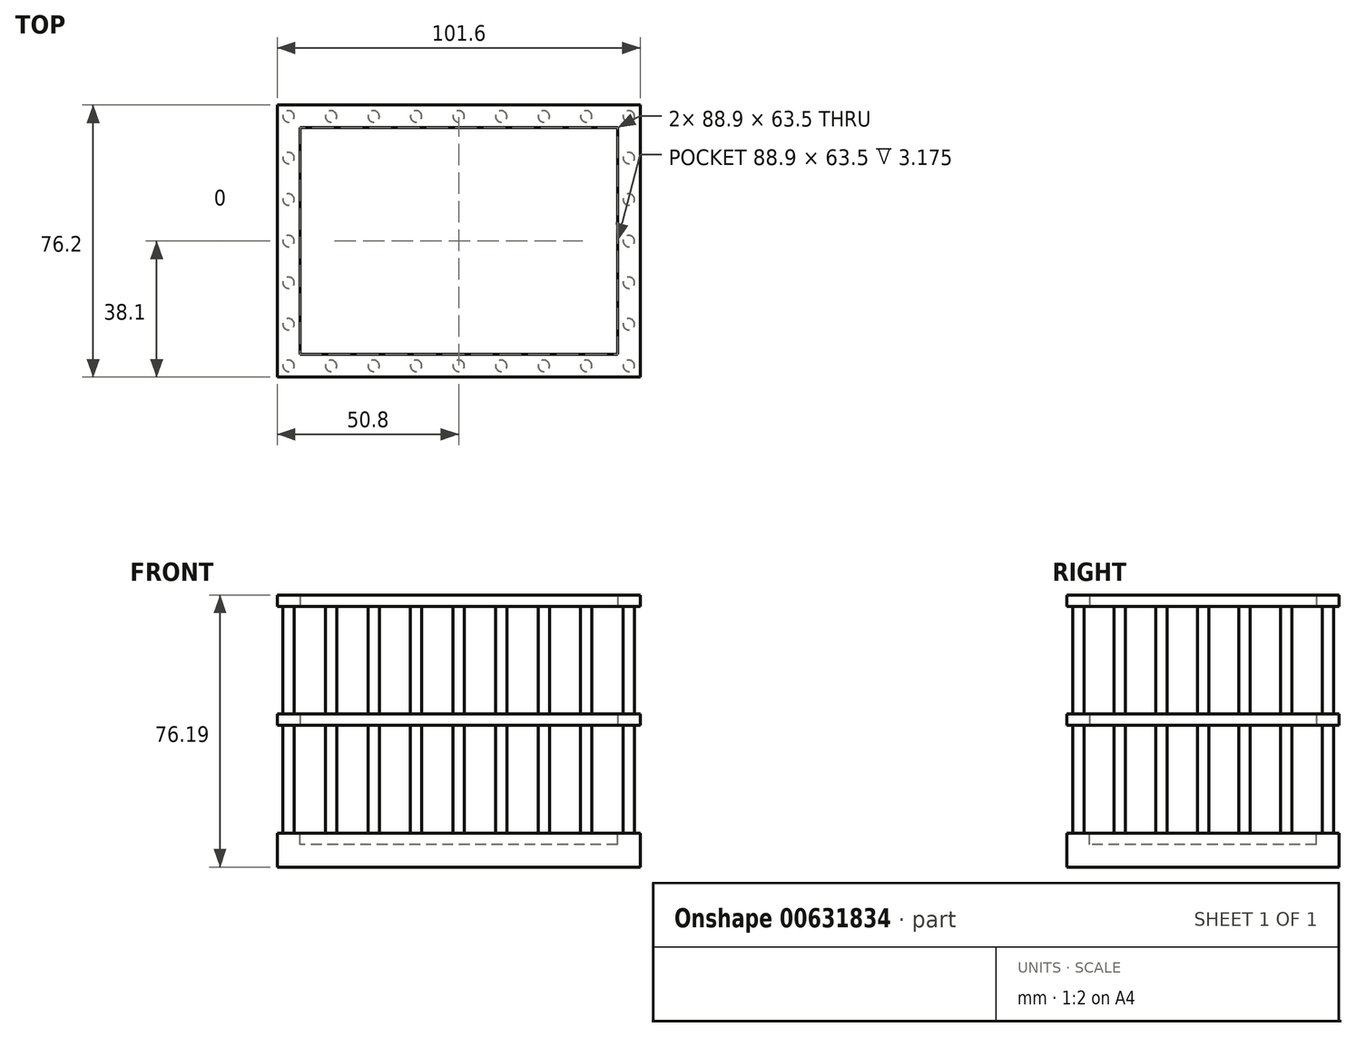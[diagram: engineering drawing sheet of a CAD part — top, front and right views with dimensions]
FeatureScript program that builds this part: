
annotation { "Feature Type Name" : "Feature", "Feature Type Description" : "" }
export const myFeature = defineFeature(function(context is Context, id is Id, definition is map)
    precondition{}
    {
        {
            var Q0;
            Q0=qCreatedBy(makeId("Top.planeOp"),FACE);
            var sketch = newSketch(context, id + "F0", { "sketchPlane" : qUnion([Q0])});
            skLineSegment(sketch, "E0.bottom", {"start": v(-101.6, 76.2) * mm, "end": v(0, 76.2) * mm});
            skLineSegment(sketch, "E0.top", {"start": v(-101.6, 0) * mm, "end": v(0, 0) * mm});
            skLineSegment(sketch, "E0.left", {"start": v(-101.6, 76.2) * mm, "end": v(-101.6, 0) * mm});
            skLineSegment(sketch, "E0.right", {"start": v(0, 76.2) * mm, "end": v(0, 0) * mm});
            skLineSegment(sketch, "E1.bottom", {"start": v(-95.25, 69.85) * mm, "end": v(-6.35, 69.85) * mm});
            skLineSegment(sketch, "E1.top", {"start": v(-95.25, 6.35) * mm, "end": v(-6.35, 6.35) * mm});
            skLineSegment(sketch, "E1.left", {"start": v(-95.25, 69.85) * mm, "end": v(-95.25, 6.35) * mm});
            skLineSegment(sketch, "E1.right", {"start": v(-6.35, 69.85) * mm, "end": v(-6.35, 6.35) * mm});
            skLineSegment(sketch, "E2", {"start": v(-95.25, 6.35) * mm, "end": v(-6.35, 69.85) * mm, "construction": true});
            skLineSegment(sketch, "E3", {"start": v(-101.6, 76.2) * mm, "end": v(0, 0) * mm, "construction": true});
            skPoint(sketch, "E4", {"position": v(-50.8, 38.1) * mm});
            skLineSegment(sketch, "E5", {"start": v(-95.25, 38.1) * mm, "end": v(-101.6, 38.1) * mm, "construction": true});
            skLineSegment(sketch, "E6", {"start": v(-50.8, 69.85) * mm, "end": v(-50.8, 76.2) * mm, "construction": true});
            skSolve(sketch);
        }
        {
            var Q0;
            Q0 = qSketchRegion(id + "F0", true);
            extrude(context, id + "F1", {"entities" : qUnion([Q0]), "endBound" : BoundingType.SYMMETRIC, "depth" : 3.17 * mm, "offsetDistance" : 25.4 * mm});
        }
        {
            var Q0;
            Q0=qCreatedBy(makeId("Top.planeOp"),FACE);
            var sketch = newSketch(context, id + "F2", { "sketchPlane" : qUnion([Q0])});
            skCircle(sketch, "E7", {"center": v(-98.42, 3.18) * mm, "radius": 1.59 * mm});
            skCircle(sketch, "E8", {"center": v(-86.52, 3.18) * mm, "radius": 1.59 * mm});
            skCircle(sketch, "E9", {"center": v(-74.61, 3.18) * mm, "radius": 1.59 * mm});
            skCircle(sketch, "E10", {"center": v(-38.9, 73.02) * mm, "radius": 1.59 * mm});
            skCircle(sketch, "E11", {"center": v(-98.42, 26.46) * mm, "radius": 1.59 * mm});
            skCircle(sketch, "E12", {"center": v(-98.42, 14.82) * mm, "radius": 1.59 * mm});
            skCircle(sketch, "E13", {"center": v(-62.7, 73.02) * mm, "radius": 1.59 * mm});
            skCircle(sketch, "E14", {"center": v(-3.17, 49.74) * mm, "radius": 1.59 * mm});
            skCircle(sketch, "E15", {"center": v(-3.17, 61.38) * mm, "radius": 1.59 * mm});
            skCircle(sketch, "E16", {"center": v(-3.17, 73.02) * mm, "radius": 1.59 * mm});
            skCircle(sketch, "E17", {"center": v(-15.08, 73.02) * mm, "radius": 1.59 * mm});
            skCircle(sketch, "E18", {"center": v(-50.8, 3.18) * mm, "radius": 1.59 * mm});
            skCircle(sketch, "E19", {"center": v(-62.7, 3.18) * mm, "radius": 1.59 * mm});
            skCircle(sketch, "E20", {"center": v(-26.99, 73.02) * mm, "radius": 1.59 * mm});
            skCircle(sketch, "E21", {"center": v(-3.17, 14.82) * mm, "radius": 1.59 * mm});
            skCircle(sketch, "E22", {"center": v(-3.17, 26.46) * mm, "radius": 1.59 * mm});
            skCircle(sketch, "E23", {"center": v(-3.17, 38.1) * mm, "radius": 1.59 * mm});
            skCircle(sketch, "E24", {"center": v(-3.17, 3.18) * mm, "radius": 1.59 * mm});
            skCircle(sketch, "E25", {"center": v(-15.08, 3.18) * mm, "radius": 1.59 * mm});
            skCircle(sketch, "E26", {"center": v(-26.99, 3.18) * mm, "radius": 1.59 * mm});
            skCircle(sketch, "E27", {"center": v(-38.9, 3.18) * mm, "radius": 1.59 * mm});
            skCircle(sketch, "E28", {"center": v(-98.43, 49.74) * mm, "radius": 1.59 * mm});
            skCircle(sketch, "E29", {"center": v(-74.61, 73.02) * mm, "radius": 1.59 * mm});
            skCircle(sketch, "E30", {"center": v(-98.43, 38.1) * mm, "radius": 1.59 * mm});
            skCircle(sketch, "E31", {"center": v(-50.8, 73.02) * mm, "radius": 1.59 * mm});
            skCircle(sketch, "E32", {"center": v(-98.42, 73.02) * mm, "radius": 1.59 * mm});
            skCircle(sketch, "E33", {"center": v(-86.52, 73.02) * mm, "radius": 1.59 * mm});
            skCircle(sketch, "E34", {"center": v(-98.43, 61.38) * mm, "radius": 1.59 * mm});
            skLineSegment(sketch, "E35", {"start": v(-98.43, 73.02) * mm, "end": v(-98.43, 61.38) * mm, "construction": true});
            skLineSegment(sketch, "E36", {"start": v(-98.43, 61.38) * mm, "end": v(-98.43, 49.74) * mm, "construction": true});
            skLineSegment(sketch, "E37", {"start": v(-98.43, 49.74) * mm, "end": v(-98.43, 38.1) * mm, "construction": true});
            skLineSegment(sketch, "E38", {"start": v(-98.43, 38.1) * mm, "end": v(-98.43, 26.46) * mm, "construction": true});
            skLineSegment(sketch, "E39", {"start": v(-98.43, 26.46) * mm, "end": v(-98.43, 14.82) * mm, "construction": true});
            skLineSegment(sketch, "E40", {"start": v(-98.43, 14.82) * mm, "end": v(-98.43, 3.18) * mm, "construction": true});
            skLineSegment(sketch, "E41", {"start": v(-3.17, 73.02) * mm, "end": v(-3.17, 61.38) * mm, "construction": true});
            skLineSegment(sketch, "E42", {"start": v(-3.17, 61.38) * mm, "end": v(-3.17, 49.74) * mm, "construction": true});
            skLineSegment(sketch, "E43", {"start": v(-3.17, 49.74) * mm, "end": v(-3.17, 38.1) * mm, "construction": true});
            skLineSegment(sketch, "E44", {"start": v(-3.17, 38.1) * mm, "end": v(-3.17, 26.46) * mm, "construction": true});
            skLineSegment(sketch, "E45", {"start": v(-3.17, 26.46) * mm, "end": v(-3.17, 14.82) * mm, "construction": true});
            skLineSegment(sketch, "E46", {"start": v(-3.17, 14.82) * mm, "end": v(-3.17, 3.18) * mm, "construction": true});
            skLineSegment(sketch, "E47", {"start": v(-3.17, 3.18) * mm, "end": v(-15.08, 3.18) * mm, "construction": true});
            skLineSegment(sketch, "E48", {"start": v(-15.08, 3.18) * mm, "end": v(-26.99, 3.18) * mm, "construction": true});
            skLineSegment(sketch, "E49", {"start": v(-26.99, 3.18) * mm, "end": v(-38.9, 3.18) * mm, "construction": true});
            skLineSegment(sketch, "E50", {"start": v(-38.9, 3.18) * mm, "end": v(-50.8, 3.18) * mm, "construction": true});
            skLineSegment(sketch, "E51", {"start": v(-50.8, 3.18) * mm, "end": v(-62.7, 3.18) * mm, "construction": true});
            skLineSegment(sketch, "E52", {"start": v(-62.7, 3.18) * mm, "end": v(-74.61, 3.18) * mm, "construction": true});
            skLineSegment(sketch, "E53", {"start": v(-86.52, 3.18) * mm, "end": v(-98.42, 3.18) * mm, "construction": true});
            skLineSegment(sketch, "E54", {"start": v(-74.61, 3.18) * mm, "end": v(-86.52, 3.18) * mm, "construction": true});
            skLineSegment(sketch, "E55", {"start": v(-3.17, 73.02) * mm, "end": v(-15.08, 73.02) * mm, "construction": true});
            skLineSegment(sketch, "E56", {"start": v(-15.08, 73.02) * mm, "end": v(-26.99, 73.02) * mm, "construction": true});
            skLineSegment(sketch, "E57", {"start": v(-26.99, 73.02) * mm, "end": v(-38.9, 73.02) * mm, "construction": true});
            skLineSegment(sketch, "E58", {"start": v(-50.8, 73.02) * mm, "end": v(-62.7, 73.02) * mm, "construction": true});
            skLineSegment(sketch, "E59", {"start": v(-62.7, 73.02) * mm, "end": v(-74.61, 73.02) * mm, "construction": true});
            skLineSegment(sketch, "E60", {"start": v(-74.61, 73.02) * mm, "end": v(-86.52, 73.02) * mm, "construction": true});
            skLineSegment(sketch, "E61", {"start": v(-86.52, 73.02) * mm, "end": v(-98.42, 73.02) * mm, "construction": true});
            skLineSegment(sketch, "E62", {"start": v(-38.9, 73.02) * mm, "end": v(-50.8, 73.02) * mm, "construction": true});
            skLineSegment(sketch, "E63", {"start": v(-50.8, 0) * mm, "end": v(-50.8, 6.35) * mm, "construction": true});
            skLineSegment(sketch, "E64", {"start": v(-95.25, 38.1) * mm, "end": v(-101.6, 38.1) * mm, "construction": true});
            skSolve(sketch);
        }
        {
            var Q0;
            Q0 = qSketchRegion(id + "F2", true);
            extrude(context, id + "F3", {"entities" : qUnion([Q0]), "operationType" : NewBodyOperationType.ADD, "endBound" : BoundingType.SYMMETRIC, "depth" : 63.5 * mm, "offsetDistance" : 25.4 * mm});
        }
        {
            var Q0;
            Q0=makeQuery(id+"F3.opExtrude","CAP_FACE",FACE,{"disambiguationData":[OSD([sQuery(id+"F2.wireOp",EDGE,"E11")])],"isStart":false});
            var sketch = newSketch(context, id + "F4", { "sketchPlane" : qUnion([Q0])});
            skLineSegment(sketch, "E65.bottom", {"start": v(0, 76.2) * mm, "end": v(-101.6, 76.2) * mm});
            skLineSegment(sketch, "E65.top", {"start": v(0, 0) * mm, "end": v(-101.6, 0) * mm});
            skLineSegment(sketch, "E65.left", {"start": v(0, 76.2) * mm, "end": v(0, 0) * mm});
            skLineSegment(sketch, "E65.right", {"start": v(-101.6, 76.2) * mm, "end": v(-101.6, 0) * mm});
            skLineSegment(sketch, "E66.bottom", {"start": v(-6.35, 6.35) * mm, "end": v(-95.25, 6.35) * mm});
            skLineSegment(sketch, "E66.top", {"start": v(-6.35, 69.85) * mm, "end": v(-95.25, 69.85) * mm});
            skLineSegment(sketch, "E66.left", {"start": v(-6.35, 6.35) * mm, "end": v(-6.35, 69.85) * mm});
            skLineSegment(sketch, "E66.right", {"start": v(-95.25, 6.35) * mm, "end": v(-95.25, 69.85) * mm});
            skLineSegment(sketch, "E67", {"start": v(-6.35, 6.35) * mm, "end": v(-95.25, 69.85) * mm, "construction": true});
            skLineSegment(sketch, "E68", {"start": v(-101.6, 0) * mm, "end": v(0, 76.2) * mm, "construction": true});
            skPoint(sketch, "E69", {"position": v(-50.8, 38.1) * mm});
            skLineSegment(sketch, "E70", {"start": v(-50.8, 6.35) * mm, "end": v(-50.8, 0) * mm, "construction": true});
            skLineSegment(sketch, "E71", {"start": v(-95.25, 38.1) * mm, "end": v(-101.6, 38.1) * mm, "construction": true});
            skPoint(sketch, "E72", {"position": v(-50.8, 3.18) * mm});
            skPoint(sketch, "E73", {"position": v(-98.43, 38.1) * mm});
            skSolve(sketch);
        }
        {
            var Q0;
            Q0 = qSketchRegion(id + "F4", true);
            extrude(context, id + "F5", {"entities" : qUnion([Q0]), "operationType" : NewBodyOperationType.ADD, "depth" : 3.17 * mm, "offsetDistance" : 25.4 * mm});
        }
        {
            var Q0;
            Q0=makeQuery(id+"F3.opExtrude","CAP_FACE",FACE,{"disambiguationData":[OSD([sQuery(id+"F2.wireOp",EDGE,"E11")])],"isStart":true});
            var sketch = newSketch(context, id + "F6", { "sketchPlane" : qUnion([Q0])});
            skLineSegment(sketch, "E74.bottom", {"start": v(0, -76.2) * mm, "end": v(-101.6, -76.2) * mm});
            skLineSegment(sketch, "E74.top", {"start": v(0, 0) * mm, "end": v(-101.6, 0) * mm});
            skLineSegment(sketch, "E74.left", {"start": v(0, -76.2) * mm, "end": v(0, 0) * mm});
            skLineSegment(sketch, "E74.right", {"start": v(-101.6, -76.2) * mm, "end": v(-101.6, 0) * mm});
            skLineSegment(sketch, "E75.bottom", {"start": v(-6.35, -69.85) * mm, "end": v(-95.25, -69.85) * mm});
            skLineSegment(sketch, "E75.top", {"start": v(-6.35, -6.35) * mm, "end": v(-95.25, -6.35) * mm});
            skLineSegment(sketch, "E75.left", {"start": v(-6.35, -69.85) * mm, "end": v(-6.35, -6.35) * mm});
            skLineSegment(sketch, "E75.right", {"start": v(-95.25, -69.85) * mm, "end": v(-95.25, -6.35) * mm});
            skLineSegment(sketch, "E76", {"start": v(0, 0) * mm, "end": v(-101.6, -76.2) * mm, "construction": true});
            skLineSegment(sketch, "E77", {"start": v(-6.35, -69.85) * mm, "end": v(-95.25, -6.35) * mm, "construction": true});
            skPoint(sketch, "E78", {"position": v(-50.8, -38.1) * mm});
            skLineSegment(sketch, "E79", {"start": v(-50.8, -69.85) * mm, "end": v(-50.8, -76.2) * mm, "construction": true});
            skPoint(sketch, "E80", {"position": v(-50.8, -73.02) * mm});
            skSolve(sketch);
        }
        {
            var Q0;
            Q0 = qSketchRegion(id + "F6", true);
            extrude(context, id + "F7", {"entities" : qUnion([Q0]), "operationType" : NewBodyOperationType.ADD, "depth" : 3.17 * mm, "offsetDistance" : 25.4 * mm});
        }
        {
            var Q0;
            Q0=makeQuery(id+"F7.opExtrude","CAP_FACE",FACE,{"disambiguationData":[OSD([sQuery(id+"F6.wireOp",EDGE,"E74.bottom"),sQuery(id+"F6.wireOp",EDGE,"E74.top"),sQuery(id+"F6.wireOp",EDGE,"E74.left"),sQuery(id+"F6.wireOp",EDGE,"E74.right"),sQuery(id+"F6.wireOp",EDGE,"E75.bottom"),sQuery(id+"F6.wireOp",EDGE,"E75.top"),sQuery(id+"F6.wireOp",EDGE,"E75.left"),sQuery(id+"F6.wireOp",EDGE,"E75.right")])],"isStart":false});
            var sketch = newSketch(context, id + "F8", { "sketchPlane" : qUnion([Q0])});
            skLineSegment(sketch, "E81.bottom", {"start": v(0, -76.2) * mm, "end": v(-101.6, -76.2) * mm});
            skLineSegment(sketch, "E81.top", {"start": v(0, 0) * mm, "end": v(-101.6, 0) * mm});
            skLineSegment(sketch, "E81.left", {"start": v(0, -76.2) * mm, "end": v(0, 0) * mm});
            skLineSegment(sketch, "E81.right", {"start": v(-101.6, -76.2) * mm, "end": v(-101.6, 0) * mm});
            skSolve(sketch);
        }
        {
            var Q0;
            Q0 = qSketchRegion(id + "F8", true);
            extrude(context, id + "F9", {"entities" : qUnion([Q0]), "operationType" : NewBodyOperationType.ADD, "depth" : 6.35 * mm, "offsetDistance" : 25.4 * mm});
        }
    });
